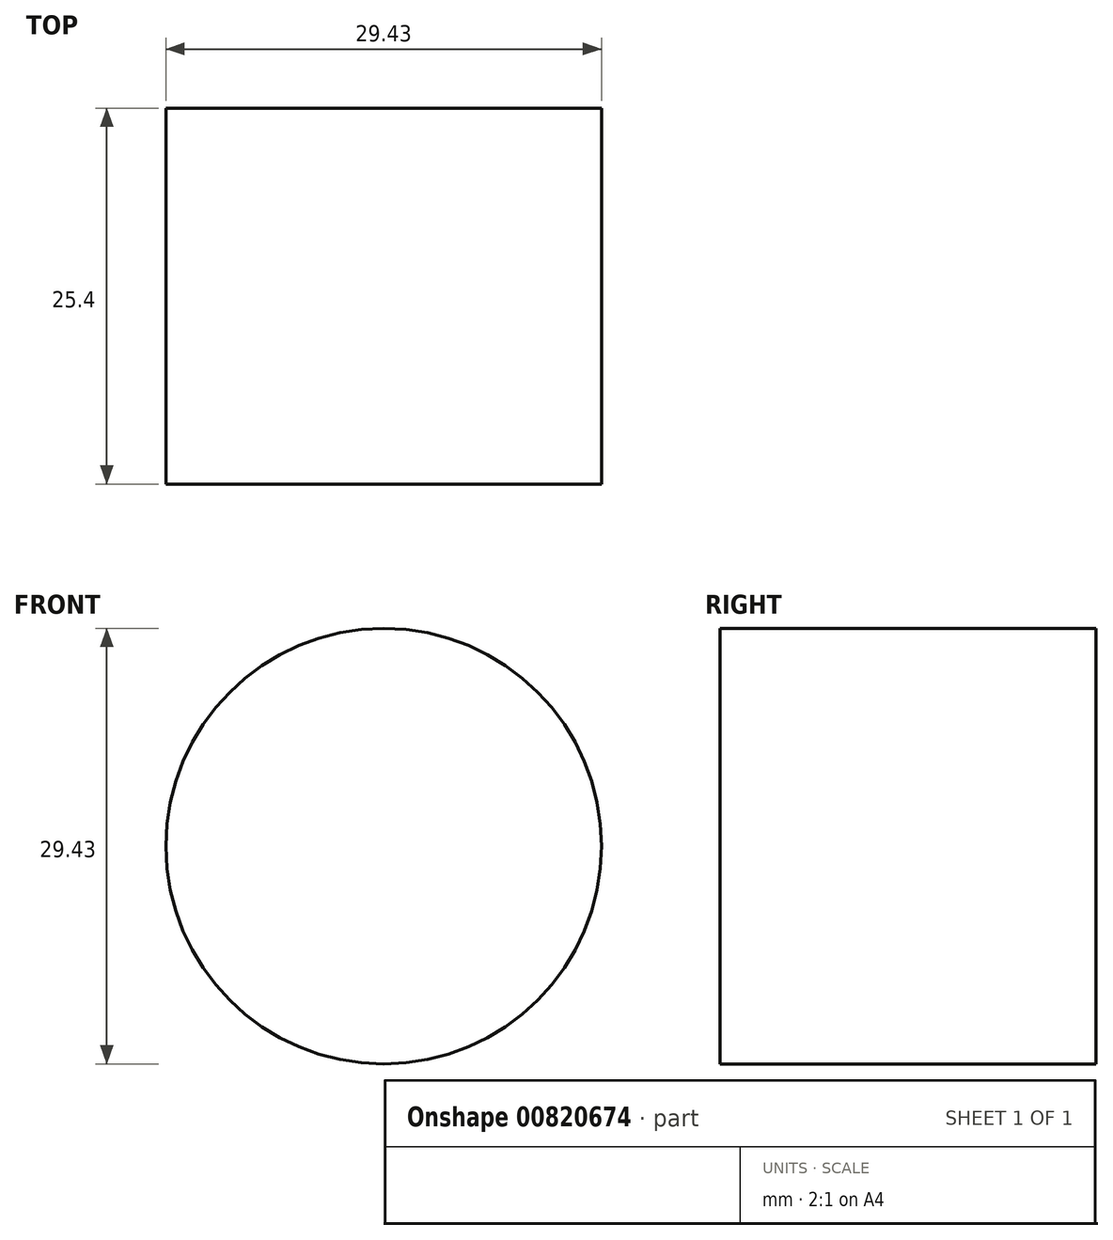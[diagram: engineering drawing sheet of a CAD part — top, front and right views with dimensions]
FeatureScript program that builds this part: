
annotation { "Feature Type Name" : "Feature", "Feature Type Description" : "" }
export const myFeature = defineFeature(function(context is Context, id is Id, definition is map)
    precondition{}
    {
        {
            var Q0;
            Q0=qCreatedBy(makeId("Front.planeOp"),FACE);
            var sketch = newSketch(context, id + "F0", { "sketchPlane" : qUnion([Q0])});
            skCircle(sketch, "E0", {"center": v(-28.12, 15.8) * mm, "radius": 14.71 * mm});
            skSolve(sketch);
        }
        {
            var Q0;
            Q0=makeQuery(id+"F0.imprint","IMPRINT",FACE,{"disambiguationData":[TD([[makeQuery(id+"F0.imprint","IMPRINT",EDGE,{"derivedFrom":sQuery(id+"F0.wireOp",EDGE,"E0")}),1.0]])]});
            extrude(context, id + "F1", {"entities" : qUnion([Q0]), "depth" : 25.4 * mm, "offsetDistance" : 25.4 * mm});
        }
    });
